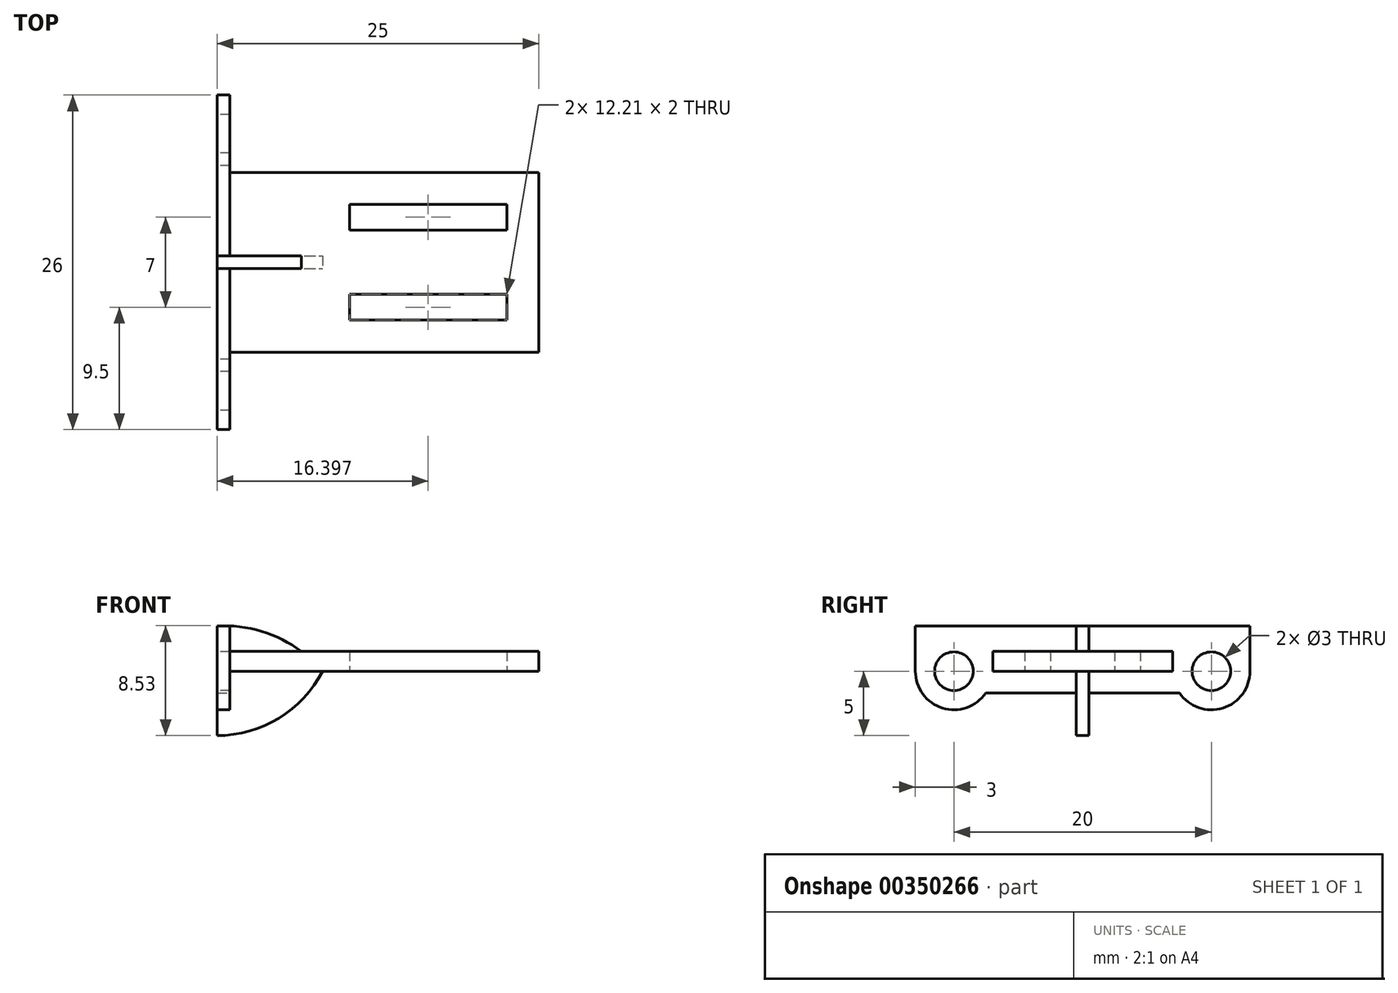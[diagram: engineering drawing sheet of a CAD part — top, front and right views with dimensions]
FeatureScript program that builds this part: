
annotation { "Feature Type Name" : "Feature", "Feature Type Description" : "" }
export const myFeature = defineFeature(function(context is Context, id is Id, definition is map)
    precondition{}
    {
        {
            var Q0;
            Q0=qCreatedBy(makeId("Right.planeOp"),FACE);
            var sketch = newSketch(context, id + "F0", { "sketchPlane" : qUnion([Q0])});
            skCircle(sketch, "E0", {"center": v(10, 0) * mm, "radius": 1.5 * mm});
            skCircle(sketch, "E1", {"center": v(-10, 0) * mm, "radius": 1.5 * mm});
            skArc(sketch, "E2", {"start": v(7.53, -1.7) * mm, "mid": v(10.9, -2.86) * mm, "end": v(13, 0) * mm});
            skLineSegment(sketch, "E3", {"start": v(13, 0) * mm, "end": v(13, 3.5) * mm});
            skPoint(sketch, "E4.trimOffspring.start.orphan", {"position": v(0, -1.42) * mm});
            skArc(sketch, "E5.MirrorCS", {"start": v(-7.53, -1.7) * mm, "mid": v(-10.9, -2.86) * mm, "end": v(-13, 0) * mm});
            skLineSegment(sketch, "E6.MirrorCS", {"start": v(-13, 0) * mm, "end": v(-13, 3.5) * mm});
            skLineSegment(sketch, "E7", {"start": v(-7.53, -1.7) * mm, "end": v(7.53, -1.7) * mm});
            skLineSegment(sketch, "E8", {"start": v(-13, 3.5) * mm, "end": v(13, 3.5) * mm});
            skPoint(sketch, "E9.bottom.start.orphan", {"position": v(-13, 7) * mm});
            skPoint(sketch, "E10.orphan", {"position": v(13, 7) * mm});
            skLineSegment(sketch, "E11", {"start": v(10, 9.64) * mm, "end": v(10, -5.42) * mm, "construction": true});
            skPoint(sketch, "E12.orphan", {"position": v(-13, 5.5) * mm});
            skPoint(sketch, "E13.end.orphan", {"position": v(0, 5.5) * mm});
            skPoint(sketch, "E13.start.orphan", {"position": v(0, 3.5) * mm});
            skPoint(sketch, "E14.end.orphan", {"position": v(13, 5.5) * mm});
            skLineSegment(sketch, "E15.bottom", {"start": v(0, 0) * mm, "end": v(6.99, 0) * mm});
            skLineSegment(sketch, "E15.top", {"start": v(0, 1.55) * mm, "end": v(6.99, 1.55) * mm});
            skLineSegment(sketch, "E15.left", {"start": v(0, 0) * mm, "end": v(0, 1.55) * mm});
            skLineSegment(sketch, "E15.right", {"start": v(6.99, 0) * mm, "end": v(6.99, 1.55) * mm});
            skLineSegment(sketch, "E16.MirrorCS", {"start": v(-6.99, 0) * mm, "end": v(-6.99, 1.55) * mm});
            skLineSegment(sketch, "E17.MirrorCS", {"start": v(0, 0) * mm, "end": v(-6.99, 0) * mm});
            skLineSegment(sketch, "E18.MirrorCS", {"start": v(0, 1.55) * mm, "end": v(-6.99, 1.55) * mm});
            skSolve(sketch);
        }
        {
            var Q0;
            Q0=makeQuery(id+"F0.imprint","IMPRINT",FACE,{"disambiguationData":[TD([[makeQuery(id+"F0.imprint","IMPRINT",EDGE,{"derivedFrom":sQuery(id+"F0.wireOp",EDGE,"E0")}),-1.0]])]});
            var Q1;
            Q1=makeQuery(id+"F0.imprint","IMPRINT",FACE,{"disambiguationData":[TD([[makeQuery(id+"F0.imprint","IMPRINT",EDGE,{"derivedFrom":sQuery(id+"F0.wireOp",EDGE,"E15.bottom")}),1.0]])]});
            extrude(context, id + "F1", {"entities" : qUnion([Q0, Q1]), "depth" : 1 * mm});
        }
        {
            var Q0;
            Q0=makeQuery(id+"F0.imprint","IMPRINT",FACE,{"disambiguationData":[TD([[makeQuery(id+"F0.imprint","IMPRINT",EDGE,{"derivedFrom":sQuery(id+"F0.wireOp",EDGE,"E15.bottom")}),1.0]])]});
            extrude(context, id + "F2", {"entities" : qUnion([Q0]), "operationType" : NewBodyOperationType.ADD, "depth" : 25 * mm});
        }
        {
            var Q0;
            Q0=makeQuery(id+"F2.opExtrude","SWEPT_FACE",FACE,{"disambiguationData":[OSD([sQuery(id+"F0.wireOp",EDGE,"E15.bottom")])]});
            var sketch = newSketch(context, id + "F3", { "sketchPlane" : qUnion([Q0])});
            skLineSegment(sketch, "E19.bottom", {"start": v(10.3, -2.5) * mm, "end": v(22.5, -2.5) * mm});
            skLineSegment(sketch, "E19.top", {"start": v(10.3, -4.5) * mm, "end": v(22.5, -4.5) * mm});
            skLineSegment(sketch, "E19.left", {"start": v(10.3, -2.5) * mm, "end": v(10.3, -4.5) * mm});
            skLineSegment(sketch, "E19.right", {"start": v(22.5, -2.5) * mm, "end": v(22.5, -4.5) * mm});
            skLineSegment(sketch, "E20.MirrorCS", {"start": v(22.5, 2.5) * mm, "end": v(22.5, 4.5) * mm});
            skLineSegment(sketch, "E21.MirrorCS", {"start": v(10.3, 2.5) * mm, "end": v(10.3, 4.5) * mm});
            skLineSegment(sketch, "E22.MirrorCS", {"start": v(10.3, 4.5) * mm, "end": v(22.5, 4.5) * mm});
            skLineSegment(sketch, "E23.MirrorCS", {"start": v(10.3, 2.5) * mm, "end": v(22.5, 2.5) * mm});
            skSolve(sketch);
        }
        {
            var Q0;
            Q0=makeQuery(id+"F3.imprint","IMPRINT",FACE,{"disambiguationData":[TD([[makeQuery(id+"F3.imprint","IMPRINT",EDGE,{"derivedFrom":sQuery(id+"F3.wireOp",EDGE,"E19.bottom")}),-1.0]])]});
            extrude(context, id + "F4", {"entities" : qUnion([Q0]), "operationType" : NewBodyOperationType.REMOVE, "oppositeDirection" : true, "depth" : 25 * mm});
        }
        {
            var Q0;
            Q0=makeQuery(id+"F2.opExtrude","SWEPT_FACE",FACE,{"disambiguationData":[OSD([sQuery(id+"F0.wireOp",EDGE,"E15.left")])]});
            var sketch = newSketch(context, id + "F5", { "sketchPlane" : qUnion([Q0])});
            skLineSegment(sketch, "E24.bottom", {"start": v(8.18, 0) * mm, "end": v(0, 0) * mm});
            skLineSegment(sketch, "E24.right", {"start": v(0, 0) * mm, "end": v(0, -5) * mm});
            skArc(sketch, "E25", {"start": v(0, -5) * mm, "mid": v(4.8, -3.65) * mm, "end": v(8.18, 0) * mm});
            skArc(sketch, "E26", {"start": v(8.18, 0) * mm, "mid": v(4.5, 2.71) * mm, "end": v(0, 3.51) * mm});
            skLineSegment(sketch, "E27", {"start": v(0, 3.51) * mm, "end": v(0, 0) * mm});
            skSolve(sketch);
        }
        {
            var Q0;
            Q0 = qSketchRegion(id + "F5", true);
            extrude(context, id + "F6", {"entities" : qUnion([Q0]), "operationType" : NewBodyOperationType.ADD, "endBound" : BoundingType.SYMMETRIC, "oppositeDirection" : true, "depth" : 1 * mm});
        }
        {
            var Q0;
            Q0=makeQuery(id+"F0.imprint","IMPRINT",FACE,{"disambiguationData":[TD([[makeQuery(id+"F0.imprint","IMPRINT",EDGE,{"derivedFrom":sQuery(id+"F0.wireOp",EDGE,"E15.left")}),1.0]])]});
            extrude(context, id + "F7", {"entities" : qUnion([Q0]), "operationType" : NewBodyOperationType.ADD, "depth" : 25 * mm});
        }
        {
            var Q0;
            Q0=makeQuery(id+"F3.imprint","IMPRINT",FACE,{"disambiguationData":[TD([[makeQuery(id+"F3.imprint","IMPRINT",EDGE,{"derivedFrom":sQuery(id+"F3.wireOp",EDGE,"E20.MirrorCS")}),1.0]])]});
            extrude(context, id + "F8", {"entities" : qUnion([Q0]), "operationType" : NewBodyOperationType.REMOVE, "oppositeDirection" : true, "depth" : 25 * mm});
        }
    });
